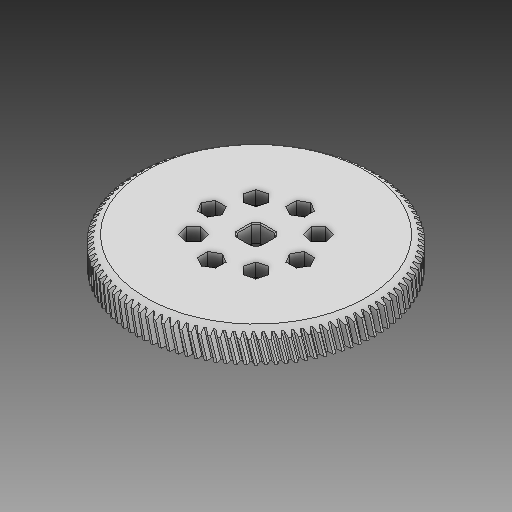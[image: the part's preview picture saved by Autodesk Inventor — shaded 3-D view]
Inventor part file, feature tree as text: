
AUTODESK INVENTOR PART (.ipt)
format: ipt  version: 2020 (Build 240168000, 168)  size: 1,542,656 bytes
history: native  units: mm
features: sketch x4, extrude x3, other x2, chamfer x2, revolve x1
ambient origin geometry x8: Origin, YZ Plane, XZ Plane, XY Plane, X Axis, Y Axis, Z Axis, Center Point
bodies: Solid1 (feature_tree)
feature tree (12):
  sketch  "Sketch1"  dims[d8=5.0mm d11=6.0mm]
  revolve  "Revolution1"  [1 undecoded]
  extrude  "Extrusion1"  Depth=10.0mm
  extrude  "Extrusion2"  Depth=8.0mm
  extrude  "Extrusion3"  Depth=10.0mm
  other  "Spur Gear Teeth1"
  chamfer  "Chamfer1"  Distance=80.0mm Angle=360.0deg
  chamfer  "Chamfer2"  [1 undecoded]
  sketch  "Sketch2"  dims[d13=10.0mm d15=54.0mm]
  sketch  "Sketch3"  dims[d16=90.0deg d21=8.0mm]
  sketch  "Sketch4"  dims[d22=20.0mm d23=5.5mm d24=80.0mm d26=360.0deg d28=0.0mm d29=0.0mm d30=8.2mm d31=80.0mm d33=360.0deg d35=6.0mm d36=0.0mm d37=6.1mm d38=8.0mm d39=0.5mm d40=2.0mm d41=45.0deg d42=27.0mm d43=3.5mm d44=3.0mm d45=24.95mm d46=10.25mm d47=10.25mm d48=10.0mm d49=0.0mm d50=34.9mm d51=0.8mm d52=47.6mm d53=0.5mm d54=21.816616mm d55=0.5mm d56=2.0mm d57=45.0deg]
  other  "Spur Gear1"
note: 2 required parameter values undecoded (feature->parameter linkage not recoverable at this tier; creation-order binding heuristic only, values carry confidence <= 0.55)